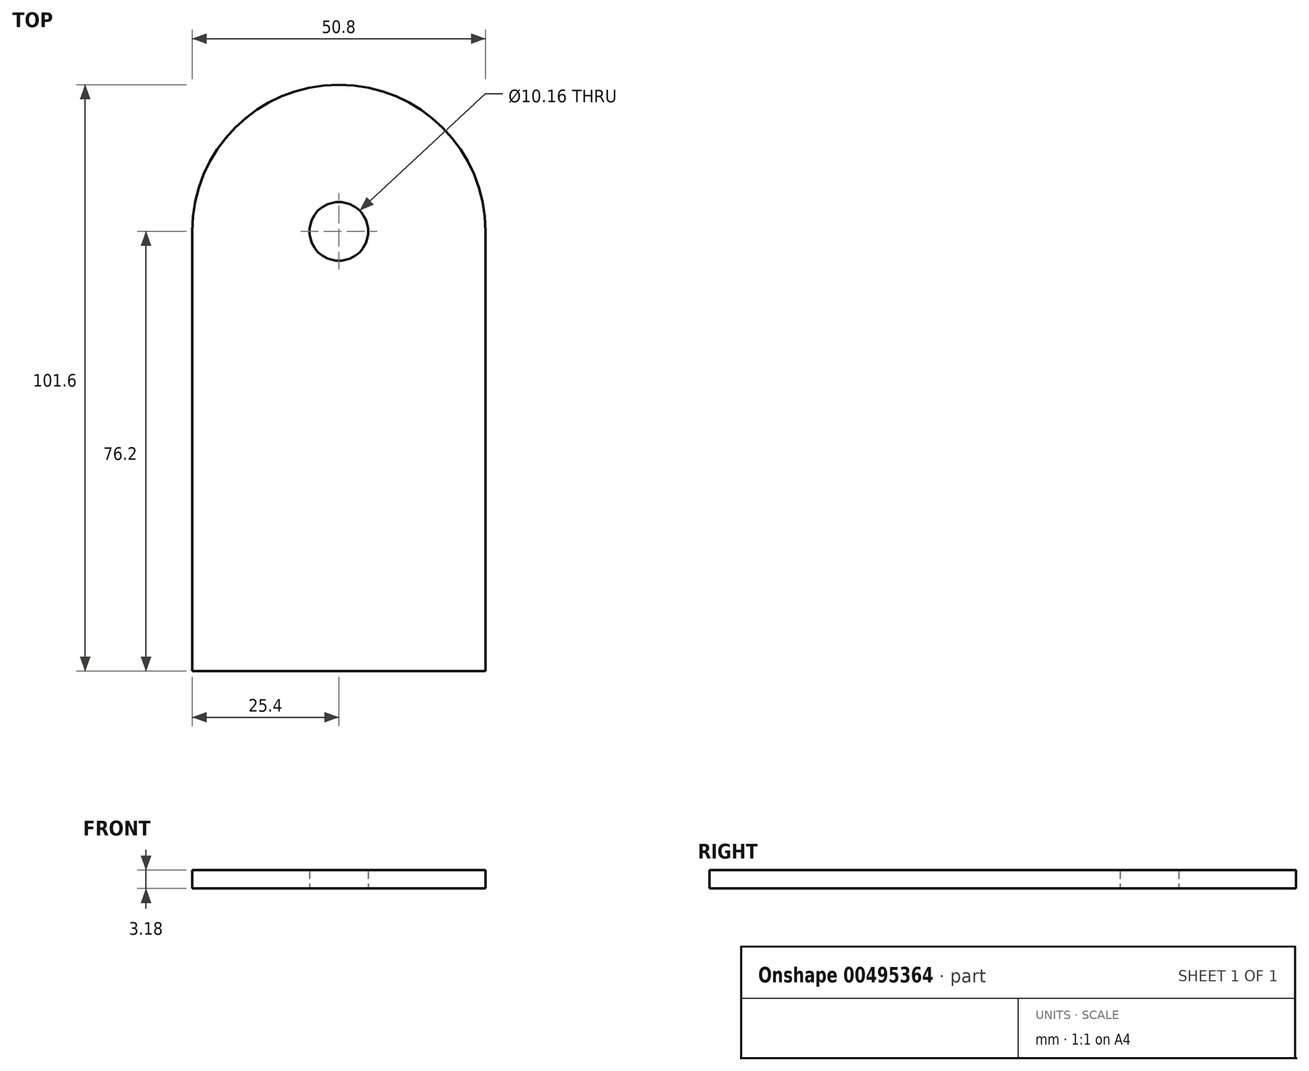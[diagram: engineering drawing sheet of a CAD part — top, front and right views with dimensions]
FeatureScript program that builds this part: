
annotation { "Feature Type Name" : "Feature", "Feature Type Description" : "" }
export const myFeature = defineFeature(function(context is Context, id is Id, definition is map)
    precondition{}
    {
        {
            var Q0;
            Q0=qCreatedBy(makeId("Top.planeOp"),FACE);
            var sketch = newSketch(context, id + "F0", { "sketchPlane" : qUnion([Q0])});
            skLineSegment(sketch, "E0.bottom", {"start": v(0, 0) * mm, "end": v(50.8, 0) * mm});
            skLineSegment(sketch, "E0.left", {"start": v(0, 0) * mm, "end": v(0, 76.2) * mm});
            skLineSegment(sketch, "E0.right", {"start": v(50.8, 0) * mm, "end": v(50.8, 76.2) * mm});
            skArc(sketch, "E1", {"start": v(0, 76.2) * mm, "mid": v(25.4, 101.6) * mm, "end": v(50.8, 76.2) * mm});
            skCircle(sketch, "E2", {"center": v(25.4, 76.2) * mm, "radius": 5.08 * mm});
            skSolve(sketch);
        }
        {
            var Q0;
            Q0=makeQuery(id+"F0.imprint","IMPRINT",FACE,{"disambiguationData":[TD([[makeQuery(id+"F0.imprint","IMPRINT",EDGE,{"derivedFrom":sQuery(id+"F0.wireOp",EDGE,"E0.bottom")}),1.0]])]});
            extrude(context, id + "F1", {"entities" : qUnion([Q0]), "depth" : 3.17 * mm});
        }
    });
